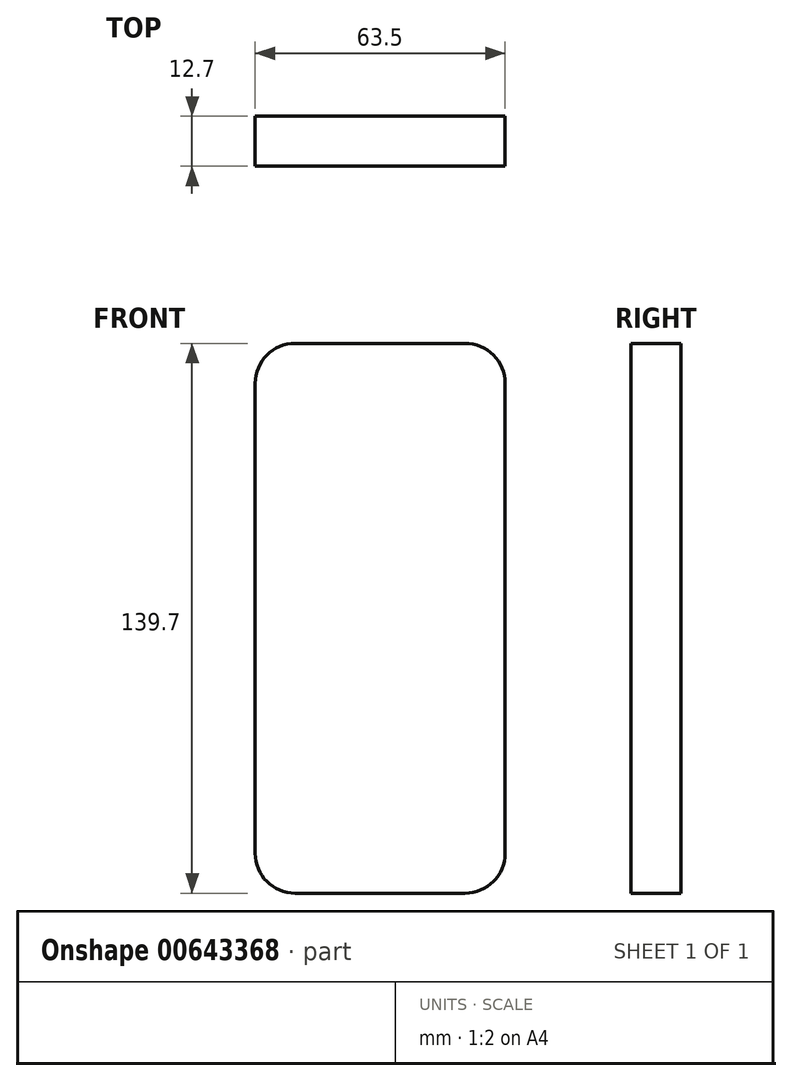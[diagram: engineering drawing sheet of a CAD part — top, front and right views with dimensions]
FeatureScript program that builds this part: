
annotation { "Feature Type Name" : "Feature", "Feature Type Description" : "" }
export const myFeature = defineFeature(function(context is Context, id is Id, definition is map)
    precondition{}
    {
        {
            var Q0;
            Q0=qCreatedBy(makeId("Front.planeOp"),FACE);
            var sketch = newSketch(context, id + "F0", { "sketchPlane" : qUnion([Q0])});
            skLineSegment(sketch, "E0.bottom", {"start": v(0, 0) * mm, "end": v(63.5, 0) * mm});
            skLineSegment(sketch, "E0.top", {"start": v(0, 139.7) * mm, "end": v(63.5, 139.7) * mm});
            skLineSegment(sketch, "E0.left", {"start": v(0, 0) * mm, "end": v(0, 139.7) * mm});
            skLineSegment(sketch, "E0.right", {"start": v(63.5, 0) * mm, "end": v(63.5, 139.7) * mm});
            skSolve(sketch);
        }
        {
            var Q0;
            Q0=makeQuery(id+"F0.imprint","IMPRINT",FACE,{"disambiguationData":[TD([[makeQuery(id+"F0.imprint","IMPRINT",EDGE,{"derivedFrom":sQuery(id+"F0.wireOp",EDGE,"E0.bottom")}),1.0]])]});
            extrude(context, id + "F1", {"entities" : qUnion([Q0]), "oppositeDirection" : true, "depth" : 12.7 * mm, "offsetDistance" : 25.4 * mm});
        }
        {
            var Q0;
            Q0=makeQuery(id+"F1.opExtrude","SWEPT_EDGE",EDGE,{"disambiguationData":[OSD([sQuery(id+"F0.wireOp",EDGE,"E0.top"),sQuery(id+"F0.wireOp",EDGE,"E0.right")])]});
            fillet(context, id + "F2", {"entities" : qUnion([Q0]), "radius" : 10.16 * mm, "tangentPropagation" : true, "allowEdgeOverflow" : false});
        }
        {
            var Q0;
            Q0=makeQuery(id+"F1.opExtrude","SWEPT_EDGE",EDGE,{"disambiguationData":[OSD([sQuery(id+"F0.wireOp",EDGE,"E0.bottom"),sQuery(id+"F0.wireOp",EDGE,"E0.right")])]});
            fillet(context, id + "F3", {"entities" : qUnion([Q0]), "radius" : 10.16 * mm, "tangentPropagation" : true, "allowEdgeOverflow" : false});
        }
        {
            var Q0;
            Q0=makeQuery(id+"F1.opExtrude","SWEPT_EDGE",EDGE,{"disambiguationData":[OSD([sQuery(id+"F0.wireOp",EDGE,"E0.top"),sQuery(id+"F0.wireOp",EDGE,"E0.left")])]});
            fillet(context, id + "F4", {"entities" : qUnion([Q0]), "radius" : 10.16 * mm, "tangentPropagation" : true, "allowEdgeOverflow" : false});
        }
        {
            var Q0;
            Q0=makeQuery(id+"F1.opExtrude","SWEPT_EDGE",EDGE,{"disambiguationData":[OSD([sQuery(id+"F0.wireOp",EDGE,"E0.bottom"),sQuery(id+"F0.wireOp",EDGE,"E0.left")])]});
            fillet(context, id + "F5", {"entities" : qUnion([Q0]), "radius" : 10.16 * mm, "tangentPropagation" : true, "allowEdgeOverflow" : false});
        }
    });
